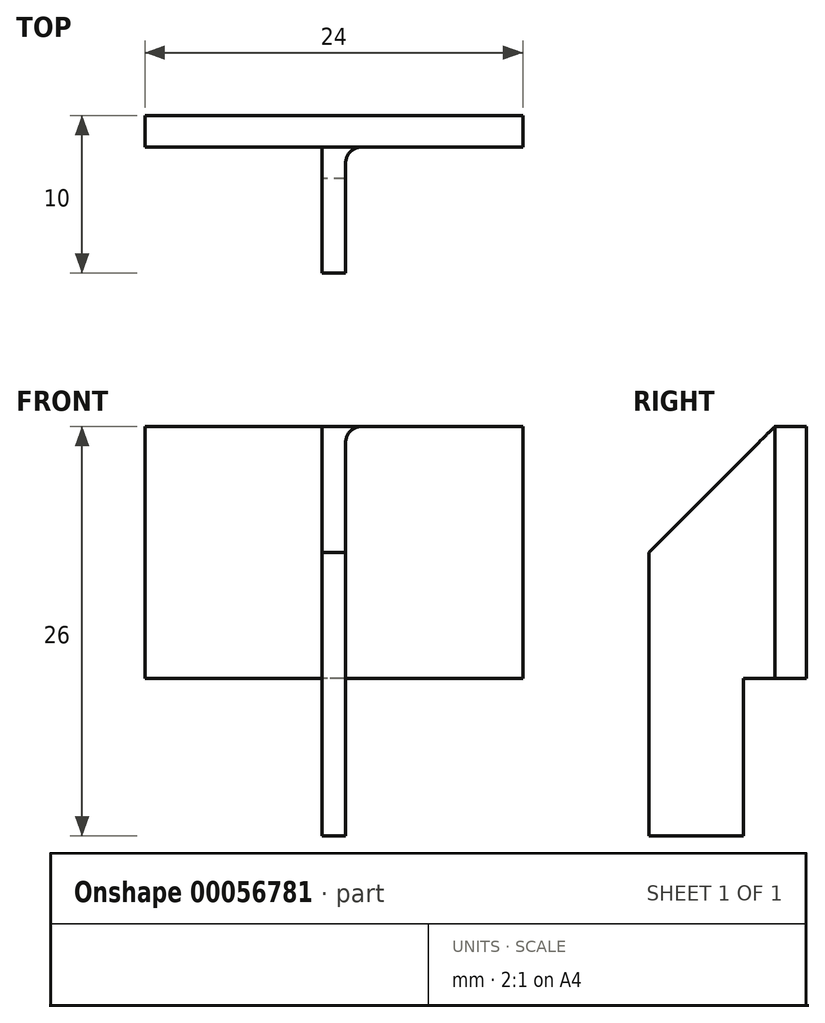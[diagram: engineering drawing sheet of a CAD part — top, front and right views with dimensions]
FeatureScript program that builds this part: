
annotation { "Feature Type Name" : "Feature", "Feature Type Description" : "" }
export const myFeature = defineFeature(function(context is Context, id is Id, definition is map)
    precondition{}
    {
        {
            var Q0;
            Q0=qCreatedBy(makeId("Front.planeOp"),FACE);
            var sketch = newSketch(context, id + "F0", { "sketchPlane" : qUnion([Q0])});
            skLineSegment(sketch, "E0.rect.bottom", {"start": v(12, 8) * mm, "end": v(-12, 8) * mm});
            skLineSegment(sketch, "E0.rect.top", {"start": v(12, -8) * mm, "end": v(-12, -8) * mm});
            skLineSegment(sketch, "E0.rect.left", {"start": v(12, 8) * mm, "end": v(12, -8) * mm});
            skLineSegment(sketch, "E0.rect.right", {"start": v(-12, 8) * mm, "end": v(-12, -8) * mm});
            skPoint(sketch, "E0.rect.middle", {"position": v(0, 0) * mm});
            skSolve(sketch);
        }
        {
            var Q0;
            Q0=qSketchRegion(id+"F0",true);
            extrude(context, id + "F1", {"entities" : qUnion([Q0]), "depth" : 2 * mm});
        }
        {
            var Q0;
            Q0=makeQuery(id+"F1.opExtrude","CAP_FACE",FACE,{"disambiguationData":[OSD([sQuery(id+"F0.wireOp",EDGE,"E0.rect.bottom"),sQuery(id+"F0.wireOp",EDGE,"E0.rect.top"),sQuery(id+"F0.wireOp",EDGE,"E0.rect.left"),sQuery(id+"F0.wireOp",EDGE,"E0.rect.right")])],"isStart":false});
            var sketch = newSketch(context, id + "F2", { "sketchPlane" : qUnion([Q0])});
            skLineSegment(sketch, "E1.rect.bottom", {"start": v(-0.75, 8) * mm, "end": v(0.75, 8) * mm});
            skLineSegment(sketch, "E1.rect.top", {"start": v(-0.75, -18) * mm, "end": v(0.75, -18) * mm});
            skLineSegment(sketch, "E1.rect.left", {"start": v(-0.75, 8) * mm, "end": v(-0.75, -18) * mm});
            skLineSegment(sketch, "E1.rect.right", {"start": v(0.75, 8) * mm, "end": v(0.75, -18) * mm});
            skPoint(sketch, "E1.rect.middle", {"position": v(0, 0) * mm});
            skLineSegment(sketch, "E2", {"start": v(0, 8) * mm, "end": v(0, 17.36) * mm, "construction": true});
            skPoint(sketch, "E2.endSnap0", {"position": v(0, 8) * mm});
            skSolve(sketch);
        }
        {
            var Q0;
            {var subQ0=sQuery(id+"F2.wireOp",EDGE,"E1.rect.bottom");Q0=makeQuery(id+"F2.imprint","IMPRINT",FACE,{"disambiguationData":[TD([[makeQuery(id+"F2.imprint","IMPRINT",EDGE,{"derivedFrom":subQ0}),1.0]])]});}
            var Q1;
            {var subQ0=sQuery(id+"F2.wireOp",EDGE,"E1.rect.top");Q1=makeQuery(id+"F2.imprint","IMPRINT",FACE,{"disambiguationData":[TD([[makeQuery(id+"F2.imprint","IMPRINT",EDGE,{"derivedFrom":subQ0}),1.0]])]});}
            extrude(context, id + "F3", {"entities" : qUnion([Q0, Q1]), "operationType" : NewBodyOperationType.ADD, "depth" : 8 * mm});
        }
        {
            var Q0;
            Q0=makeQuery(id+"F3.opExtrude","CAP_FACE",FACE,{"disambiguationData":[OSD([sQuery(id+"F2.wireOp",EDGE,"E1.rect.bottom"),sQuery(id+"F2.wireOp",EDGE,"E1.rect.top"),sQuery(id+"F2.wireOp",EDGE,"E1.rect.left"),sQuery(id+"F2.wireOp",EDGE,"E1.rect.right")])],"isStart":true});
            extrude(context, id + "F4", {"entities" : qUnion([Q0]), "operationType" : NewBodyOperationType.REMOVE, "oppositeDirection" : true, "depth" : 2 * mm});
        }
        {
            var Q0;
            Q0=makeQuery(id+"F3.opExtrude","CAP_EDGE",EDGE,{"disambiguationData":[OSD([sQuery(id+"F2.wireOp",EDGE,"E1.rect.bottom")])],"isStart":false});
            chamfer(context, id + "F5", {"entities" : qUnion([Q0]), "width" : 8 * mm, "tangentPropagation" : true});
        }
        {
            var Q0;
            {var subQ1=sQuery(id+"F0.wireOp",EDGE,"E0.rect.bottom");var subQ3=sQuery(id+"F2.wireOp",EDGE,"E1.rect.left");Q0=makeQuery(id+"F3.boolean.opBoolean","SPLIT",EDGE,{"disambiguationData":[TD([makeQuery(id+"F1.opExtrude","SWEPT_FACE",FACE,{"disambiguationData":[OSD([subQ1])]})])],"derivedFrom":makeQuery(id+"F3.opExtrude","CAP_EDGE",EDGE,{"disambiguationData":[OSD([subQ3])],"isStart":true})});}
            var Q1;
            {var subQ1=sQuery(id+"F0.wireOp",EDGE,"E0.rect.bottom");var subQ3=sQuery(id+"F2.wireOp",EDGE,"E1.rect.right");Q1=makeQuery(id+"F3.boolean.opBoolean","SPLIT",EDGE,{"disambiguationData":[TD([makeQuery(id+"F1.opExtrude","SWEPT_FACE",FACE,{"disambiguationData":[OSD([subQ1])]})])],"derivedFrom":makeQuery(id+"F3.opExtrude","CAP_EDGE",EDGE,{"disambiguationData":[OSD([subQ3])],"isStart":true})});}
            fillet(context, id + "F6", {"entities" : qUnion([Q0, Q1]), "radius" : 1 * mm, "tangentPropagation" : true, "allowEdgeOverflow" : false});
        }
    });
